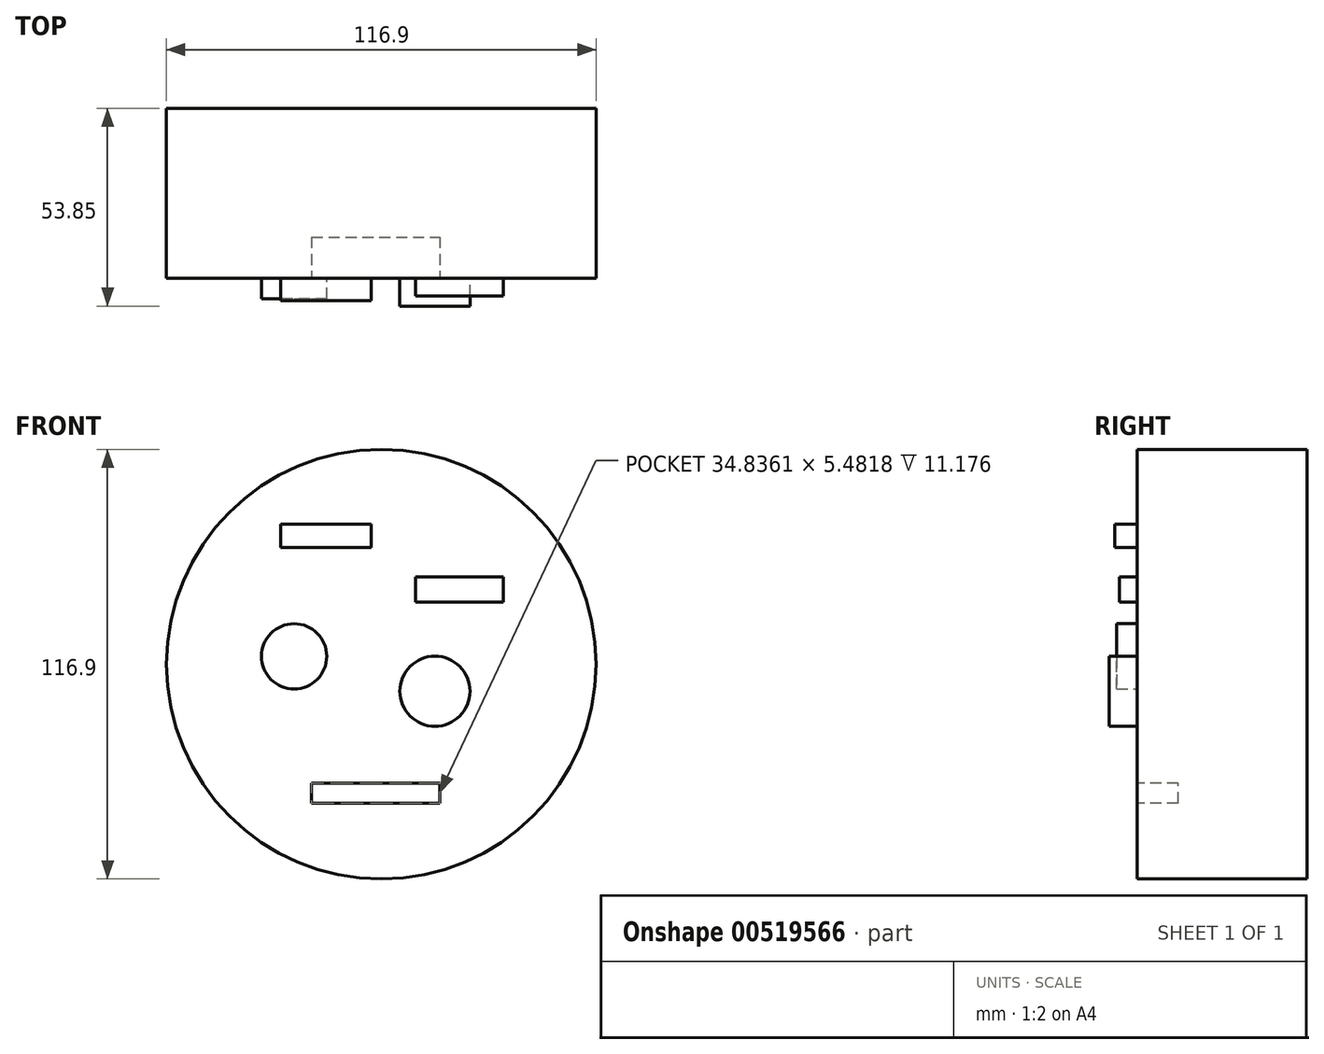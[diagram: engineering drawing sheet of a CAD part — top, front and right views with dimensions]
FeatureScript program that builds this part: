
annotation { "Feature Type Name" : "Feature", "Feature Type Description" : "" }
export const myFeature = defineFeature(function(context is Context, id is Id, definition is map)
    precondition{}
    {
        {
            var Q0;
            Q0=qCreatedBy(makeId("Front.planeOp"),FACE);
            var sketch = newSketch(context, id + "F0", { "sketchPlane" : qUnion([Q0])});
            skCircle(sketch, "E0", {"center": v(-49.33, 18.88) * mm, "radius": 58.45 * mm});
            skSolve(sketch);
        }
        {
            var Q0;
            Q0 = qSketchRegion(id + "F0", true);
            extrude(context, id + "F1", {"entities" : qUnion([Q0]), "depth" : 46.23 * mm, "offsetDistance" : 25.4 * mm});
        }
        {
            var Q0;
            Q0=makeQuery(id+"F1.opExtrude","CAP_FACE",FACE,{"disambiguationData":[OSD([sQuery(id+"F0.wireOp",EDGE,"E0")])],"isStart":false});
            var sketch = newSketch(context, id + "F2", { "sketchPlane" : qUnion([Q0])});
            skLineSegment(sketch, "E1.bottom", {"start": v(-76.68, 50.64) * mm, "end": v(-52.08, 50.64) * mm});
            skLineSegment(sketch, "E1.top", {"start": v(-76.68, 56.93) * mm, "end": v(-52.08, 56.93) * mm});
            skLineSegment(sketch, "E1.left", {"start": v(-76.68, 50.64) * mm, "end": v(-76.68, 56.93) * mm});
            skLineSegment(sketch, "E1.right", {"start": v(-52.08, 50.64) * mm, "end": v(-52.08, 56.93) * mm});
            skSolve(sketch);
        }
        {
            var Q0;
            Q0 = qSketchRegion(id + "F2", true);
            extrude(context, id + "F3", {"entities" : qUnion([Q0]), "operationType" : NewBodyOperationType.ADD, "depth" : 6.1 * mm, "offsetDistance" : 25.4 * mm});
        }
        {
            var Q0;
            Q0=makeQuery(id+"F1.opExtrude","CAP_FACE",FACE,{"disambiguationData":[OSD([sQuery(id+"F0.wireOp",EDGE,"E0")])],"isStart":false});
            var sketch = newSketch(context, id + "F4", { "sketchPlane" : qUnion([Q0])});
            skLineSegment(sketch, "E2.bottom", {"start": v(-39.98, 35.82) * mm, "end": v(-16.19, 35.82) * mm});
            skLineSegment(sketch, "E2.top", {"start": v(-39.98, 42.7) * mm, "end": v(-16.19, 42.7) * mm});
            skLineSegment(sketch, "E2.left", {"start": v(-39.98, 35.82) * mm, "end": v(-39.98, 42.7) * mm});
            skLineSegment(sketch, "E2.right", {"start": v(-16.19, 35.82) * mm, "end": v(-16.19, 42.7) * mm});
            skSolve(sketch);
        }
        {
            var Q0;
            Q0 = qSketchRegion(id + "F4", true);
            extrude(context, id + "F5", {"entities" : qUnion([Q0]), "operationType" : NewBodyOperationType.ADD, "depth" : 4.83 * mm, "offsetDistance" : 25.4 * mm});
        }
        {
            var Q0;
            Q0=makeQuery(id+"F1.opExtrude","CAP_FACE",FACE,{"disambiguationData":[OSD([sQuery(id+"F0.wireOp",EDGE,"E0")])],"isStart":false});
            var sketch = newSketch(context, id + "F6", { "sketchPlane" : qUnion([Q0])});
            skCircle(sketch, "E3", {"center": v(-73.05, 21.03) * mm, "radius": 8.88 * mm});
            skSolve(sketch);
        }
        {
            var Q0;
            Q0 = qSketchRegion(id + "F6", true);
            extrude(context, id + "F7", {"entities" : qUnion([Q0]), "operationType" : NewBodyOperationType.ADD, "depth" : 5.6 * mm, "offsetDistance" : 25.4 * mm});
        }
        {
            var Q0;
            Q0=makeQuery(id+"F1.opExtrude","CAP_FACE",FACE,{"disambiguationData":[OSD([sQuery(id+"F0.wireOp",EDGE,"E0")])],"isStart":false});
            var sketch = newSketch(context, id + "F8", { "sketchPlane" : qUnion([Q0])});
            skCircle(sketch, "E4", {"center": v(-34.74, 11.53) * mm, "radius": 9.53 * mm});
            skSolve(sketch);
        }
        {
            var Q0;
            Q0 = qSketchRegion(id + "F8", true);
            extrude(context, id + "F9", {"entities" : qUnion([Q0]), "operationType" : NewBodyOperationType.ADD, "depth" : 7.62 * mm, "offsetDistance" : 25.4 * mm});
        }
        {
            var Q0;
            Q0=makeQuery(id+"F1.opExtrude","CAP_FACE",FACE,{"disambiguationData":[OSD([sQuery(id+"F0.wireOp",EDGE,"E0")])],"isStart":false});
            var sketch = newSketch(context, id + "F10", { "sketchPlane" : qUnion([Q0])});
            skArc(sketch, "E5", {"start": v(-51.27, -32.77) * mm, "mid": v(-53.92, -4.01) * mm, "end": v(-80.31, -15.74) * mm});
            skSolve(sketch);
        }
        {
            var Q0;
            Q0 = qSketchRegion(id + "F10", true);
            var Q1;
            Q1=makeQuery(id+"F1.opExtrude","CAP_FACE",FACE,{"disambiguationData":[OSD([sQuery(id+"F0.wireOp",EDGE,"E0")])],"isStart":false});
            extrude(context, id + "F11", {"entities" : qUnion([Q0, Q1]), "operationType" : NewBodyOperationType.ADD, "oppositeDirection" : true, "depth" : 6.6 * mm, "offsetDistance" : 25.4 * mm});
        }
        {
            var Q0;
            Q0=makeQuery(id+"F1.opExtrude","CAP_FACE",FACE,{"disambiguationData":[OSD([sQuery(id+"F0.wireOp",EDGE,"E0")])],"isStart":false});
            var sketch = newSketch(context, id + "F12", { "sketchPlane" : qUnion([Q0])});
            skLineSegment(sketch, "E6.bottom", {"start": v(-68.27, -18.92) * mm, "end": v(-33.44, -18.92) * mm});
            skLineSegment(sketch, "E6.top", {"start": v(-68.27, -13.43) * mm, "end": v(-33.44, -13.43) * mm});
            skLineSegment(sketch, "E6.left", {"start": v(-68.27, -18.92) * mm, "end": v(-68.27, -13.43) * mm});
            skLineSegment(sketch, "E6.right", {"start": v(-33.44, -18.92) * mm, "end": v(-33.44, -13.43) * mm});
            skSolve(sketch);
        }
        {
            var Q0;
            Q0 = qSketchRegion(id + "F12", true);
            extrude(context, id + "F13", {"entities" : qUnion([Q0]), "operationType" : NewBodyOperationType.REMOVE, "oppositeDirection" : true, "depth" : 11.18 * mm, "offsetDistance" : 25.4 * mm});
        }
    });
